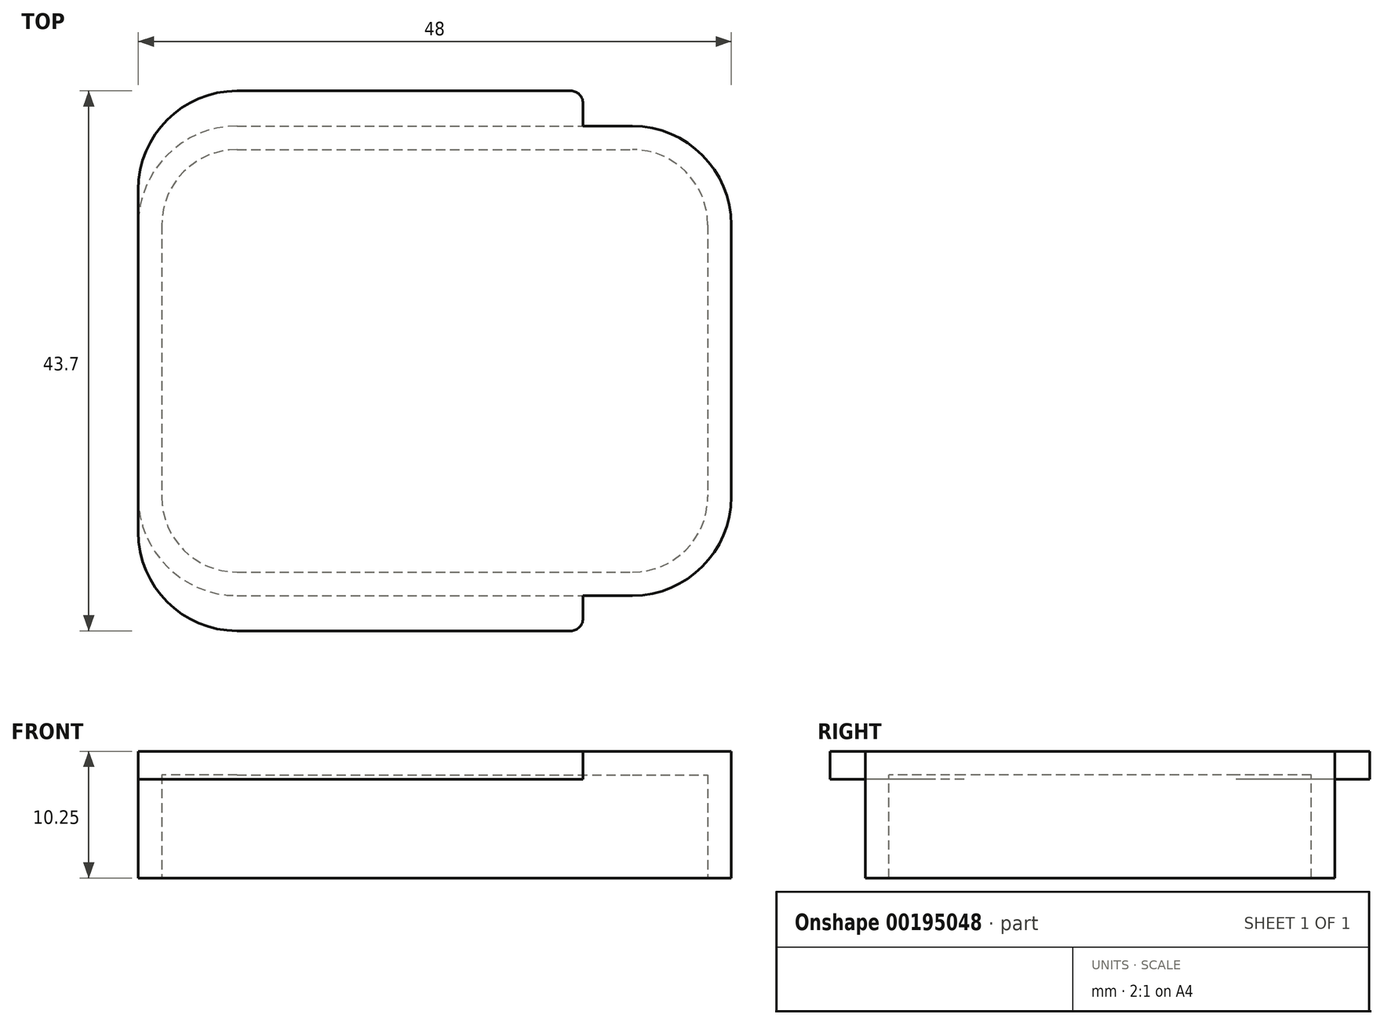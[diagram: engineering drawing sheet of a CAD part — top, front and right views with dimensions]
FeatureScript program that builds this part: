
annotation { "Feature Type Name" : "Feature", "Feature Type Description" : "" }
export const myFeature = defineFeature(function(context is Context, id is Id, definition is map)
    precondition{}
    {
        {
            var Q0;
            Q0=qCreatedBy(makeId("Top.planeOp"),FACE);
            var sketch = newSketch(context, id + "F0", { "sketchPlane" : qUnion([Q0])});
            skLineSegment(sketch, "E0.bottom", {"start": v(-16, 19) * mm, "end": v(16, 19) * mm});
            skLineSegment(sketch, "E0.top", {"start": v(-16, -19) * mm, "end": v(16, -19) * mm});
            skLineSegment(sketch, "E0.left", {"start": v(-24, 11) * mm, "end": v(-24, -11) * mm});
            skLineSegment(sketch, "E0.right", {"start": v(24, 11) * mm, "end": v(24, -11) * mm});
            skPoint(sketch, "E1.visualSharp", {"position": v(24, 19) * mm});
            skArc(sketch, "E1.filletArc", {"start": v(24, 11) * mm, "mid": v(21.66, 16.66) * mm, "end": v(16, 19) * mm});
            skPoint(sketch, "E2.visualSharp", {"position": v(-24, -19) * mm});
            skArc(sketch, "E2.filletArc", {"start": v(-24, -11) * mm, "mid": v(-21.66, -16.66) * mm, "end": v(-16, -19) * mm});
            skPoint(sketch, "E3.visualSharp", {"position": v(-24, 19) * mm});
            skArc(sketch, "E3.filletArc", {"start": v(-16, 19) * mm, "mid": v(-21.66, 16.66) * mm, "end": v(-24, 11) * mm});
            skPoint(sketch, "E4.visualSharp", {"position": v(24, -19) * mm});
            skArc(sketch, "E4.filletArc", {"start": v(16, -19) * mm, "mid": v(21.66, -16.66) * mm, "end": v(24, -11) * mm});
            skSolve(sketch);
        }
        {
            var Q0;
            Q0=makeQuery(id+"F0.imprint","IMPRINT",FACE,{"disambiguationData":[TD([[makeQuery(id+"F0.imprint","IMPRINT",EDGE,{"derivedFrom":sQuery(id+"F0.wireOp",EDGE,"E0.bottom")}),-1.0]])]});
            extrude(context, id + "F1", {"entities" : qUnion([Q0]), "depth" : 10.25 * mm});
        }
        {
            var Q0;
            Q0=makeQuery(id+"F1.opExtrude","CAP_FACE",FACE,{"disambiguationData":[OSD([sQuery(id+"F0.wireOp",EDGE,"E0.bottom"),sQuery(id+"F0.wireOp",EDGE,"E0.top"),sQuery(id+"F0.wireOp",EDGE,"E0.left"),sQuery(id+"F0.wireOp",EDGE,"E0.right"),sQuery(id+"F0.wireOp",EDGE,"E1.filletArc"),sQuery(id+"F0.wireOp",EDGE,"E2.filletArc"),sQuery(id+"F0.wireOp",EDGE,"E3.filletArc"),sQuery(id+"F0.wireOp",EDGE,"E4.filletArc")])],"isStart":true});
            shell(context, id + "F2", {"entities" : qUnion([Q0]), "thickness" : 1.9 * mm});
        }
        {
            var Q0;
            Q0=makeQuery(id+"F1.opExtrude","CAP_FACE",FACE,{"disambiguationData":[OSD([sQuery(id+"F0.wireOp",EDGE,"E0.bottom"),sQuery(id+"F0.wireOp",EDGE,"E0.top"),sQuery(id+"F0.wireOp",EDGE,"E0.left"),sQuery(id+"F0.wireOp",EDGE,"E0.right"),sQuery(id+"F0.wireOp",EDGE,"E1.filletArc"),sQuery(id+"F0.wireOp",EDGE,"E2.filletArc"),sQuery(id+"F0.wireOp",EDGE,"E3.filletArc"),sQuery(id+"F0.wireOp",EDGE,"E4.filletArc")])],"isStart":false});
            var sketch = newSketch(context, id + "F3", { "sketchPlane" : qUnion([Q0])});
            skLineSegment(sketch, "E5.bottom", {"start": v(-16, 21.85) * mm, "end": v(12, 21.85) * mm});
            skLineSegment(sketch, "E5.top", {"start": v(-16, -21.85) * mm, "end": v(12, -21.85) * mm});
            skLineSegment(sketch, "E5.left", {"start": v(-24, 13.85) * mm, "end": v(-24, -13.85) * mm});
            skLineSegment(sketch, "E5.right", {"start": v(12, 21.85) * mm, "end": v(12, -21.85) * mm});
            skPoint(sketch, "E6.visualSharp", {"position": v(-24, 21.85) * mm});
            skArc(sketch, "E6.filletArc", {"start": v(-16, 21.85) * mm, "mid": v(-21.66, 19.5) * mm, "end": v(-24, 13.85) * mm});
            skPoint(sketch, "E7.visualSharp", {"position": v(-24, -21.85) * mm});
            skArc(sketch, "E7.filletArc", {"start": v(-24, -13.85) * mm, "mid": v(-21.66, -19.5) * mm, "end": v(-16, -21.85) * mm});
            skSolve(sketch);
        }
        {
            var Q0;
            {var subQ1=sQuery(id+"F3.wireOp",EDGE,"E5.bottom");Q0=makeQuery(id+"F3.imprint","IMPRINT",FACE,{"disambiguationData":[TD([[makeQuery(id+"F3.imprint","IMPRINT",EDGE,{"derivedFrom":subQ1}),-1.0]])]});}
            var Q1;
            {var subQ1=sQuery(id+"F3.wireOp",EDGE,"E5.top");Q1=makeQuery(id+"F3.imprint","IMPRINT",FACE,{"disambiguationData":[TD([[makeQuery(id+"F3.imprint","IMPRINT",EDGE,{"derivedFrom":subQ1}),1.0]])]});}
            extrude(context, id + "F4", {"entities" : qUnion([Q0, Q1]), "operationType" : NewBodyOperationType.ADD, "oppositeDirection" : true, "depth" : 2.25 * mm});
        }
        {
            var Q0;
            Q0=makeQuery(id+"F4.opExtrude","SWEPT_EDGE",EDGE,{"disambiguationData":[OSD([sQuery(id+"F0.wireOp",EDGE,"E0.bottom"),sQuery(id+"F3.wireOp",EDGE,"E5.right")])]});
            var Q1;
            Q1=makeQuery(id+"F4.opExtrude","SWEPT_EDGE",EDGE,{"disambiguationData":[OSD([sQuery(id+"F3.wireOp",EDGE,"E5.bottom"),sQuery(id+"F3.wireOp",EDGE,"E5.right")])]});
            var Q2;
            Q2=makeQuery(id+"F4.opExtrude","SWEPT_EDGE",EDGE,{"disambiguationData":[OSD([sQuery(id+"F0.wireOp",EDGE,"E0.top"),sQuery(id+"F3.wireOp",EDGE,"E5.right")])]});
            var Q3;
            Q3=makeQuery(id+"F4.opExtrude","SWEPT_EDGE",EDGE,{"disambiguationData":[OSD([sQuery(id+"F3.wireOp",EDGE,"E5.top"),sQuery(id+"F3.wireOp",EDGE,"E5.right")])]});
            fillet(context, id + "F5", {"entities" : qUnion([Q0, Q1, Q2, Q3]), "radius" : 1 * mm, "tangentPropagation" : true, "allowEdgeOverflow" : false});
        }
    });
